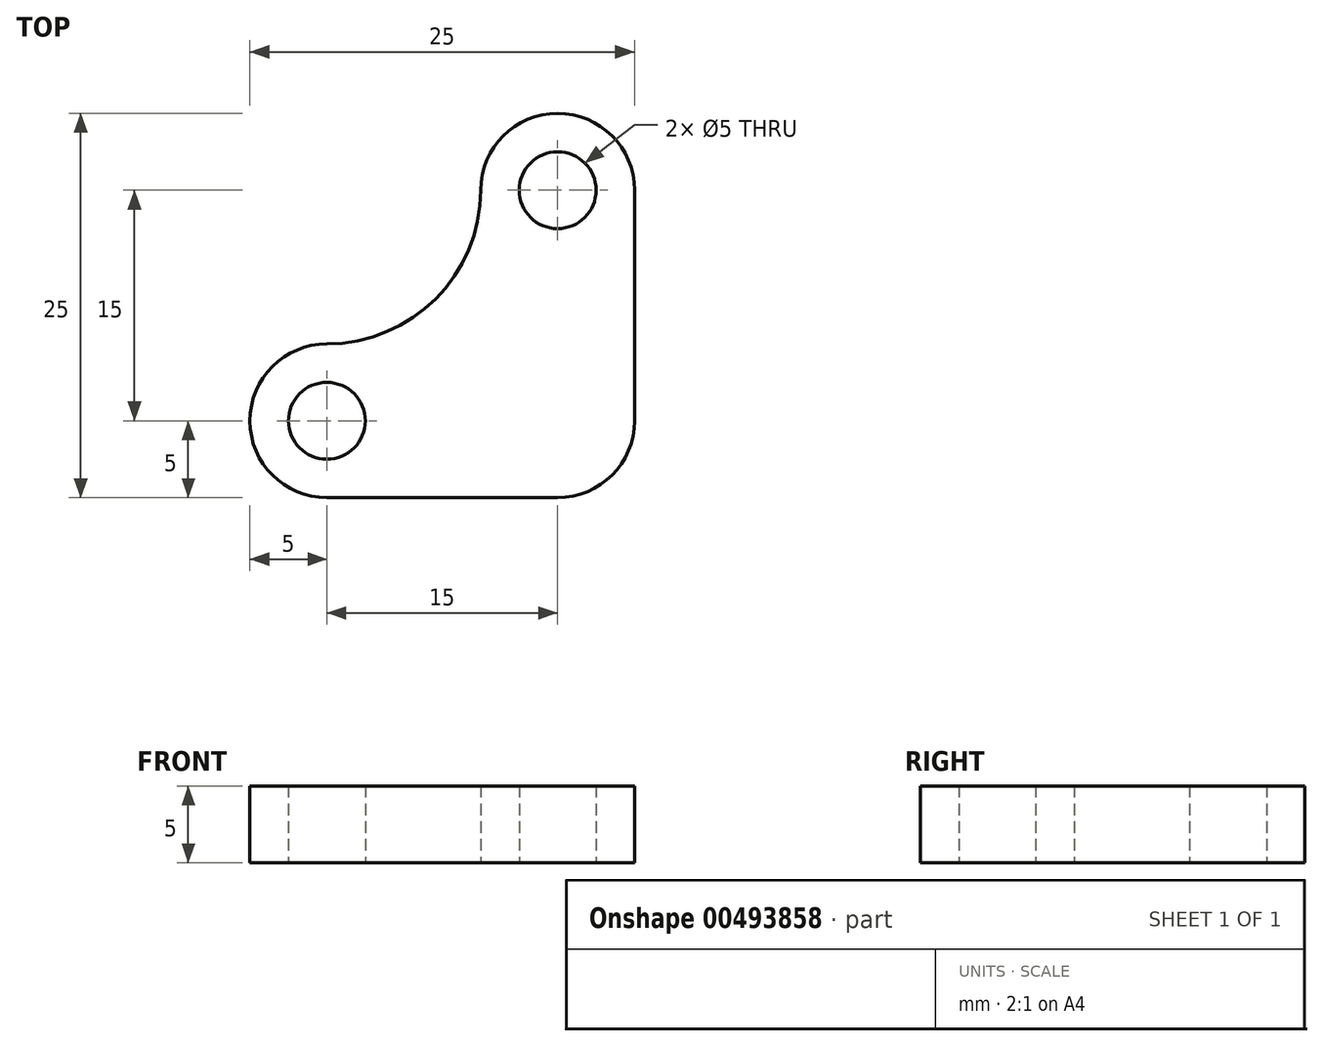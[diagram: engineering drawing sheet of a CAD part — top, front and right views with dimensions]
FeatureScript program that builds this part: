
annotation { "Feature Type Name" : "Feature", "Feature Type Description" : "" }
export const myFeature = defineFeature(function(context is Context, id is Id, definition is map)
    precondition{}
    {
        {
            var Q0;
            Q0=qCreatedBy(makeId("Top.planeOp"),FACE);
            var sketch = newSketch(context, id + "F0", { "sketchPlane" : qUnion([Q0])});
            skLineSegment(sketch, "E0", {"start": v(5, 0) * mm, "end": v(5, 15) * mm});
            skArc(sketch, "E1", {"start": v(5, 15) * mm, "mid": v(0, 20) * mm, "end": v(-5, 15) * mm});
            skArc(sketch, "E2", {"start": v(0, -5) * mm, "mid": v(3.54, -3.54) * mm, "end": v(5, 0) * mm});
            skArc(sketch, "E3", {"start": v(-15, 5) * mm, "mid": v(-7.93, 7.93) * mm, "end": v(-5, 15) * mm});
            skArc(sketch, "E4", {"start": v(-15, 5) * mm, "mid": v(-20, 0) * mm, "end": v(-15, -5) * mm});
            skCircle(sketch, "E5", {"center": v(0, 15) * mm, "radius": 2.5 * mm});
            skLineSegment(sketch, "E6", {"start": v(-15, -5) * mm, "end": v(0, -5) * mm});
            skCircle(sketch, "E7", {"center": v(-15, 0) * mm, "radius": 2.5 * mm});
            skSolve(sketch);
        }
        {
            var Q0;
            Q0=makeQuery(id+"F0.imprint","IMPRINT",FACE,{"disambiguationData":[TD([[makeQuery(id+"F0.imprint","IMPRINT",EDGE,{"derivedFrom":sQuery(id+"F0.wireOp",EDGE,"E0")}),1.0]])]});
            extrude(context, id + "F1", {"entities" : qUnion([Q0]), "depth" : 5 * mm});
        }
    });
